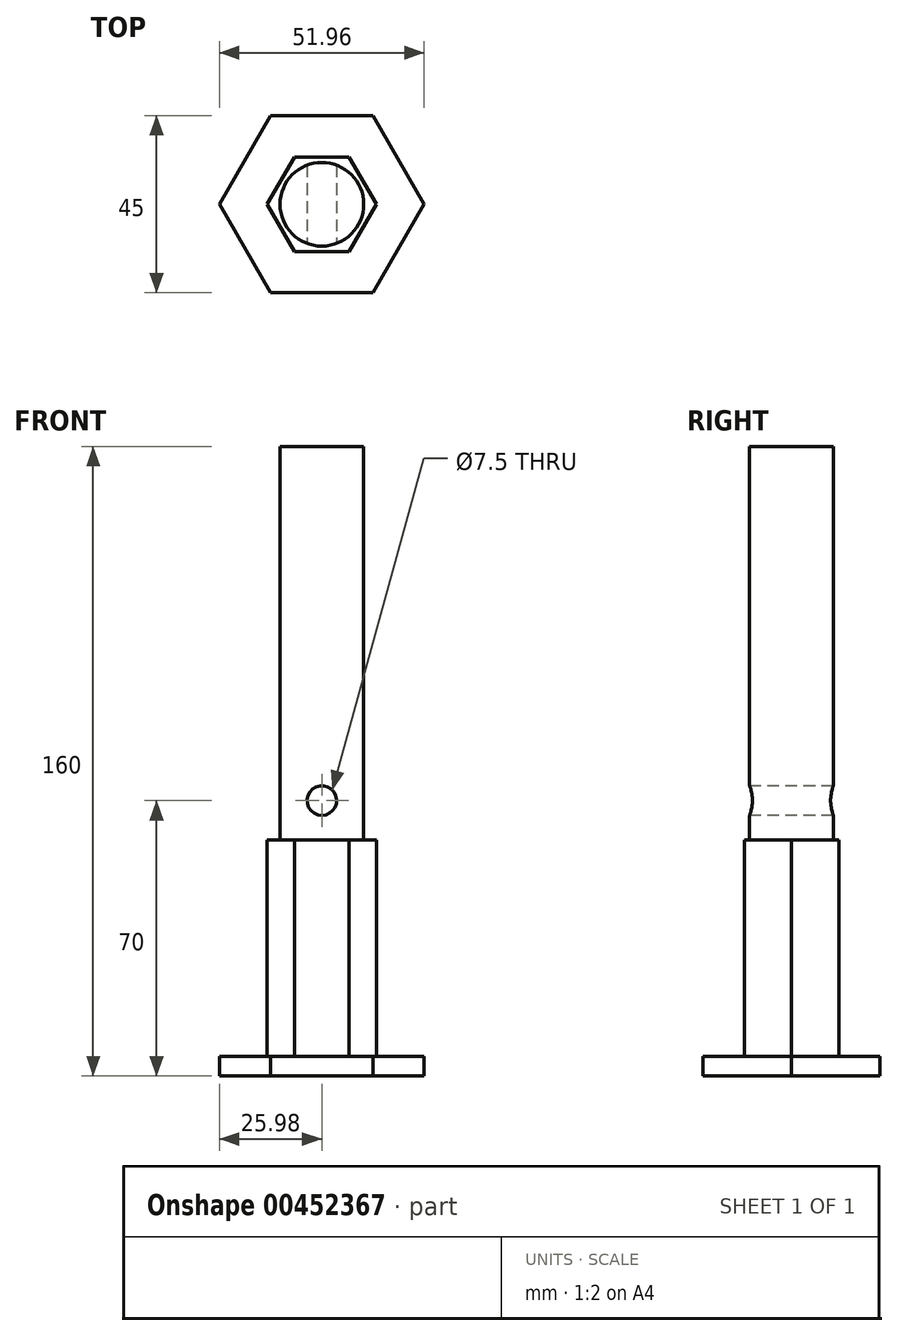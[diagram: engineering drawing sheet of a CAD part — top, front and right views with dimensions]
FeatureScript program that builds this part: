
annotation { "Feature Type Name" : "Feature", "Feature Type Description" : "" }
export const myFeature = defineFeature(function(context is Context, id is Id, definition is map)
    precondition{}
    {
        {
            var Q0;
            Q0=qCreatedBy(makeId("Top.planeOp"),FACE);
            var sketch = newSketch(context, id + "F0", { "sketchPlane" : qUnion([Q0])});
            skCircle(sketch, "E0.cCircle", {"center": v(0, 0) * mm, "radius": 12 * mm, "construction": true});
            skLineSegment(sketch, "E0.0", {"start": v(-6.93, 12) * mm, "end": v(6.93, 12) * mm});
            skLineSegment(sketch, "E0.1", {"start": v(6.93, 12) * mm, "end": v(13.86, 0) * mm});
            skLineSegment(sketch, "E0.2", {"start": v(13.86, 0) * mm, "end": v(6.93, -12) * mm});
            skLineSegment(sketch, "E0.3", {"start": v(6.93, -12) * mm, "end": v(-6.93, -12) * mm});
            skLineSegment(sketch, "E0.4", {"start": v(-6.93, -12) * mm, "end": v(-13.86, 0) * mm});
            skLineSegment(sketch, "E0.5", {"start": v(-13.86, 0) * mm, "end": v(-6.93, 12) * mm});
            skPoint(sketch, "E0.0.midPoint", {"position": v(0, 12) * mm});
            skSolve(sketch);
        }
        {
            var Q0;
            Q0=makeQuery(id+"F0.imprint","IMPRINT",FACE,{"disambiguationData":[TD([[makeQuery(id+"F0.imprint","IMPRINT",EDGE,{"derivedFrom":sQuery(id+"F0.wireOp",EDGE,"E0.0")}),-1.0]])]});
            extrude(context, id + "F1", {"entities" : qUnion([Q0]), "depth" : 160 * mm});
        }
        {
            var Q0;
            Q0=qCreatedBy(makeId("Top.planeOp"),FACE);
            var sketch = newSketch(context, id + "F2", { "sketchPlane" : qUnion([Q0])});
            skCircle(sketch, "E1.cCircle", {"center": v(0, 0) * mm, "radius": 22.5 * mm, "construction": true});
            skLineSegment(sketch, "E1.0", {"start": v(13, -22.5) * mm, "end": v(-13, -22.5) * mm});
            skLineSegment(sketch, "E1.1", {"start": v(-13, -22.5) * mm, "end": v(-25.98, 0) * mm});
            skLineSegment(sketch, "E1.2", {"start": v(-25.98, 0) * mm, "end": v(-13, 22.5) * mm});
            skLineSegment(sketch, "E1.3", {"start": v(-13, 22.5) * mm, "end": v(13, 22.5) * mm});
            skLineSegment(sketch, "E1.4", {"start": v(13, 22.5) * mm, "end": v(25.98, 0) * mm});
            skLineSegment(sketch, "E1.5", {"start": v(25.98, 0) * mm, "end": v(13, -22.5) * mm});
            skPoint(sketch, "E1.0.midPoint", {"position": v(0, -22.5) * mm});
            skSolve(sketch);
        }
        {
            var Q0;
            Q0 = qSketchRegion(id + "F2", true);
            extrude(context, id + "F3", {"entities" : qUnion([Q0]), "operationType" : NewBodyOperationType.ADD, "depth" : 5 * mm});
        }
        {
            var Q0;
            Q0=makeQuery(id+"F1.opExtrude","CAP_FACE",FACE,{"disambiguationData":[OSD([sQuery(id+"F0.wireOp",EDGE,"E0.0"),sQuery(id+"F0.wireOp",EDGE,"E0.1"),sQuery(id+"F0.wireOp",EDGE,"E0.2"),sQuery(id+"F0.wireOp",EDGE,"E0.3"),sQuery(id+"F0.wireOp",EDGE,"E0.4"),sQuery(id+"F0.wireOp",EDGE,"E0.5")])],"isStart":false});
            var sketch = newSketch(context, id + "F4", { "sketchPlane" : qUnion([Q0])});
            skCircle(sketch, "E2.cCircle", {"center": v(0, 0) * mm, "radius": 12 * mm, "construction": true});
            skLineSegment(sketch, "E2.0", {"start": v(-6.93, 12) * mm, "end": v(6.93, 12) * mm});
            skLineSegment(sketch, "E2.1", {"start": v(6.93, 12) * mm, "end": v(13.86, 0) * mm});
            skLineSegment(sketch, "E2.2", {"start": v(13.86, 0) * mm, "end": v(6.93, -12) * mm});
            skLineSegment(sketch, "E2.3", {"start": v(6.93, -12) * mm, "end": v(-6.93, -12) * mm});
            skLineSegment(sketch, "E2.4", {"start": v(-6.93, -12) * mm, "end": v(-13.86, 0) * mm});
            skLineSegment(sketch, "E2.5", {"start": v(-13.86, 0) * mm, "end": v(-6.93, 12) * mm});
            skPoint(sketch, "E2.0.midPoint", {"position": v(0, 12) * mm});
            skCircle(sketch, "E3", {"center": v(0, 0) * mm, "radius": 10.62 * mm});
            skSolve(sketch);
        }
        {
            var Q0;
            Q0 = qSketchRegion(id + "F4", true);
            extrude(context, id + "F5", {"entities" : qUnion([Q0]), "operationType" : NewBodyOperationType.REMOVE, "oppositeDirection" : true, "depth" : 100 * mm});
        }
        {
            var Q0;
            Q0=qCreatedBy(makeId("Front.planeOp"),FACE);
            var sketch = newSketch(context, id + "F6", { "sketchPlane" : qUnion([Q0])});
            skCircle(sketch, "E4", {"center": v(0, 70) * mm, "radius": 3.75 * mm});
            skSolve(sketch);
        }
        {
            var Q0;
            Q0 = qSketchRegion(id + "F6", true);
            extrude(context, id + "F7", {"entities" : qUnion([Q0]), "operationType" : NewBodyOperationType.REMOVE, "endBound" : BoundingType.SYMMETRIC, "oppositeDirection" : true, "depth" : 100 * mm});
        }
    });
